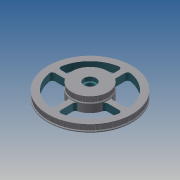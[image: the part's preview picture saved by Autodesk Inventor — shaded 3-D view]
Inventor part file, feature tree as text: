
AUTODESK INVENTOR PART (.ipt)
format: ipt  version: 2013 (Build 170138000, 138)  size: 1,565,184 bytes
history: native  units: mm
features: extrude x4, sketch x4, other x3, fillet x1, pattern_circular x1
ambient origin geometry x8: Origin, YZ Plane, XZ Plane, XY Plane, X Axis, Y Axis, Z Axis, Center Point
bodies: Solid1 (feature_tree)
feature tree (13):
  other  "z idler pulley.iam"
  other  "235 pulley blank.ipt:1"
  other  "100 pulley blank.ipt:1"
  extrude  "Extrusion1"  Depth=15.0mm
  extrude  "Extrusion2"  Depth=22.0mm
  extrude  "Extrusion3"  Depth=7.0mm TaperAngle=0.0deg
  extrude  "Extrusion4"  Depth=5.0mm
  fillet  "Fillet1"  Radius=12.0mm
  pattern_circular  "Circular Pattern1"  [2 undecoded]
  sketch  "Sketch1"  dims[d0=10.0mm d1=15.0mm]
  sketch  "Sketch2"  dims[d3=10.0mm d4=0.0mm d5=22.0mm]
  sketch  "Sketch3"  dims[d7=7.0mm d8=0.0mm d9=7.0mm d10=0.0mm]
  sketch  "Sketch4"  dims[d11=5.0mm d12=5.0mm d13=12.0mm d14=7.0mm d15=0.0mm d16=5.0mm d17=40.0mm d18=360.0deg]
note: 2 required parameter values undecoded (feature->parameter linkage not recoverable at this tier; creation-order binding heuristic only, values carry confidence <= 0.55)
